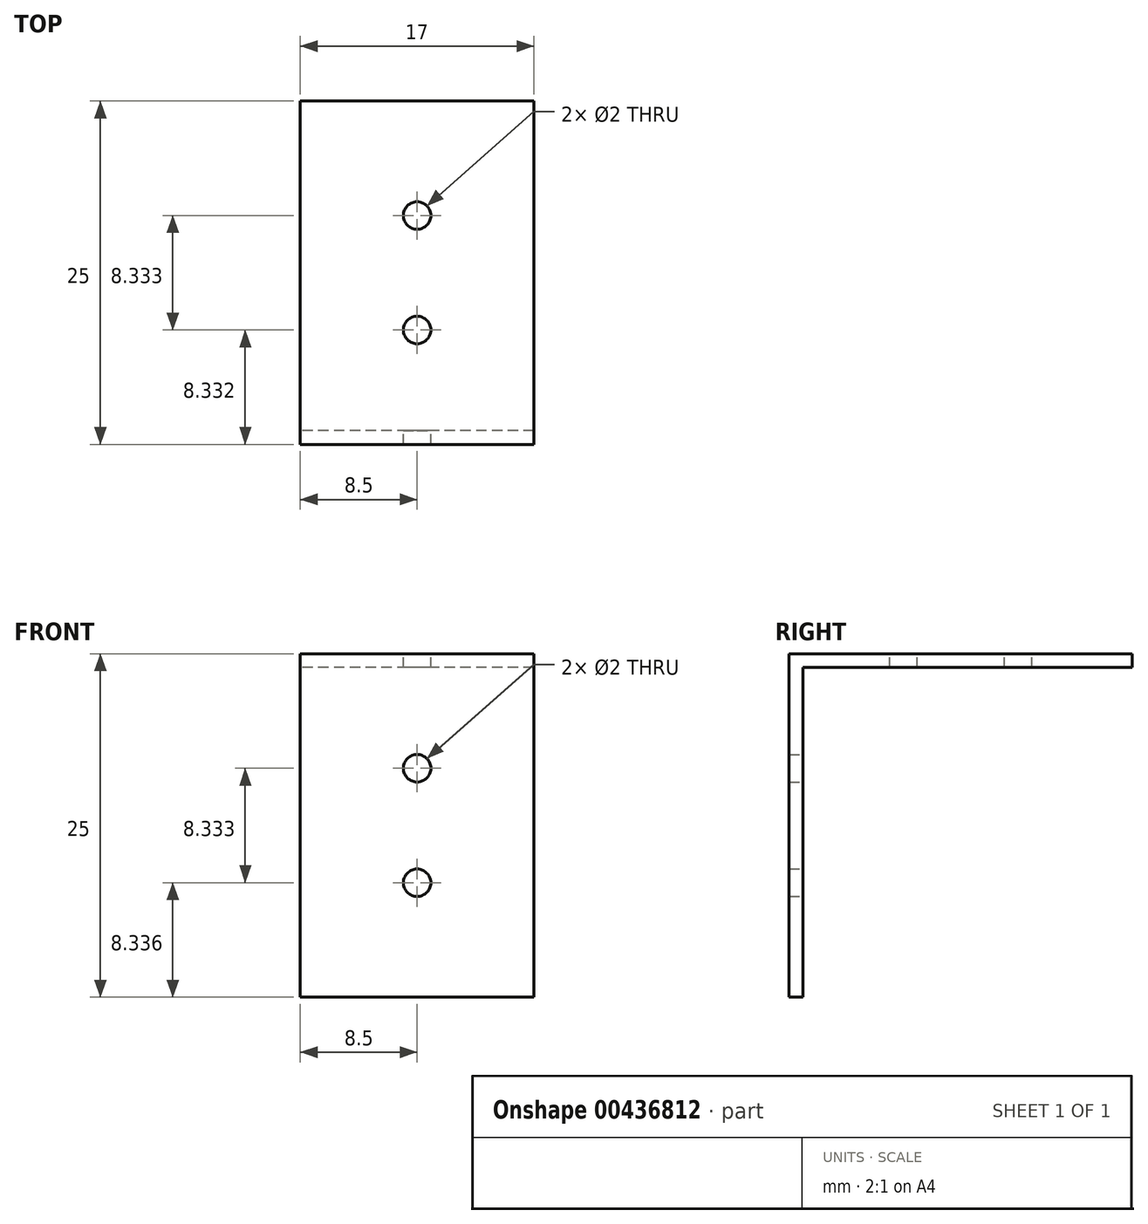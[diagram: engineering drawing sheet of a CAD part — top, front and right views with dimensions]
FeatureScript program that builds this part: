
annotation { "Feature Type Name" : "Feature", "Feature Type Description" : "" }
export const myFeature = defineFeature(function(context is Context, id is Id, definition is map)
    precondition{}
    {
        {
            var Q0;
            Q0=qCreatedBy(makeId("Right.planeOp"),FACE);
            var sketch = newSketch(context, id + "F0", { "sketchPlane" : qUnion([Q0])});
            skLineSegment(sketch, "E0.bottom", {"start": v(-98.2, 22.42) * mm, "end": v(-73.2, 22.42) * mm});
            skLineSegment(sketch, "E0.top", {"start": v(-98.2, -2.58) * mm, "end": v(-97.2, -2.58) * mm});
            skLineSegment(sketch, "E0.left", {"start": v(-98.2, 22.42) * mm, "end": v(-98.2, -2.58) * mm});
            skLineSegment(sketch, "E0.right", {"start": v(-73.2, 22.42) * mm, "end": v(-73.2, 21.42) * mm});
            skLineSegment(sketch, "E1.0", {"start": v(-97.2, 21.42) * mm, "end": v(-73.2, 21.42) * mm});
            skLineSegment(sketch, "E2.0", {"start": v(-97.2, 21.42) * mm, "end": v(-97.2, -2.58) * mm});
            skSolve(sketch);
        }
        {
            var Q0;
            Q0=makeQuery(id+"F0.imprint","IMPRINT",FACE,{"disambiguationData":[TD([[makeQuery(id+"F0.imprint","IMPRINT",EDGE,{"derivedFrom":sQuery(id+"F0.wireOp",EDGE,"E0.bottom")}),-1.0]])]});
            extrude(context, id + "F1", {"entities" : qUnion([Q0]), "depth" : 17 * mm});
        }
        {
            var Q0;
            Q0=makeQuery(id+"F1.opExtrude","SWEPT_FACE",FACE,{"disambiguationData":[OSD([sQuery(id+"F0.wireOp",EDGE,"E2.0")])]});
            var sketch = newSketch(context, id + "F2", { "sketchPlane" : qUnion([Q0])});
            skCircle(sketch, "E3", {"center": v(-8.5, 5.76) * mm, "radius": 1 * mm});
            skCircle(sketch, "E4", {"center": v(-8.5, 14.09) * mm, "radius": 1 * mm});
            skSolve(sketch);
        }
        {
            var Q0;
            Q0 = qSketchRegion(id + "F2", true);
            extrude(context, id + "F3", {"entities" : qUnion([Q0]), "operationType" : NewBodyOperationType.REMOVE, "oppositeDirection" : true, "depth" : 1 * mm});
        }
        {
            var Q0;
            Q0=makeQuery(id+"F1.opExtrude","SWEPT_FACE",FACE,{"disambiguationData":[OSD([sQuery(id+"F0.wireOp",EDGE,"E0.bottom")])]});
            var sketch = newSketch(context, id + "F4", { "sketchPlane" : qUnion([Q0])});
            skCircle(sketch, "E5", {"center": v(8.5, -81.53) * mm, "radius": 1 * mm});
            skCircle(sketch, "E6", {"center": v(8.5, -89.87) * mm, "radius": 1 * mm});
            skSolve(sketch);
        }
        {
            var Q0;
            Q0 = qSketchRegion(id + "F4", true);
            extrude(context, id + "F5", {"entities" : qUnion([Q0]), "operationType" : NewBodyOperationType.REMOVE, "oppositeDirection" : true, "depth" : 1 * mm});
        }
    });
